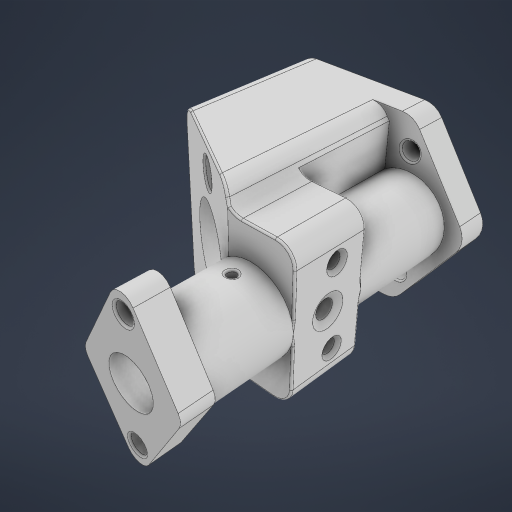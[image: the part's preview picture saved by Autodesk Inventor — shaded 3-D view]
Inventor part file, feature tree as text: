
AUTODESK INVENTOR PART (.ipt)
format: ipt  version: 2024.2 (Build 282272000, 272)  size: 712,192 bytes
history: native  units: mm
features: extrude x13, sketch x12, projected_geometry x12, fillet x9, chamfer x5, plane x1
ambient origin geometry x8: Origin, YZ Plane, XZ Plane, XY Plane, X Axis, Y Axis, Z Axis, Center Point
bodies: Solid1 (feature_tree)
feature tree (52):
  extrude  "Extrusion1"  Depth=22.5mm
  extrude  "Extrusion2"  Depth=16.134mm
  extrude  "Extrusion3"  Depth=5.0mm
  fillet  "Fillet1"  Radius=21.816616mm
  fillet  "Fillet3"  Radius=21.816616mm
  extrude  "Extrusion4"  Depth=6.0mm
  extrude  "Extrusion5"  Depth=8.0mm
  chamfer  "Chamfer1"  Distance=60.0mm
  chamfer  "Chamfer2"  Angle=120.0deg  [1 undecoded]
  chamfer  "Chamfer3"  Distance=49.469mm
  sketch  "Sketch6"  dims[d15=120.0deg]
  extrude  "Extrusion6"  Depth=0.5mm
  fillet  "Fillet4"  Radius=5.0mm
  extrude  "Extrusion7"  Depth=0.5mm
  fillet  "Fillet5"  [1 undecoded]
  sketch  "Sketch7"  dims[d16=120.0deg]
  plane  "Work Plane1"
  sketch  "Sketch8"  dims[d17=28.0mm]
  extrude  "Extrusion8"  TaperAngle=90.0deg  [1 undecoded]
  extrude  "Extrusion9"  Depth=0.5mm
  extrude  "Extrusion10"  Depth=0.5mm
  fillet  "Fillet6"  Radius=17.5mm
  chamfer  "Chamfer4"  Distance=10.0mm
  chamfer  "Chamfer5"  Distance=24.0mm
  fillet  "Fillet7"  Radius=2.5mm
  extrude  "Extrusion11"  Depth=0.5mm
  fillet  "Fillet8"  Radius=4.0mm
  fillet  "Fillet9"  Radius=7.5mm
  extrude  "Extrusion12"  Depth=0.5mm
  extrude  "Extrusion13"  Depth=0.5mm
  fillet  "Fillet10"  Radius=10.0mm
  sketch  "Sketch1"  dims[d0=12.5mm d1=22.5mm]
  sketch  "Sketch2"  dims[d2=16.134mm d3=16.134mm]
  projected_geometry  "Projected Loop1"
  sketch  "Sketch3"  dims[d4=5.0mm d5=5.0mm d6=21.816616mm d7=21.816616mm]
  projected_geometry  "Projected Loop2"
  sketch  "Sketch4"  dims[d8=40.0mm d9=6.0mm]
  projected_geometry  "Projected Loop3"
  projected_geometry  "Projected Loop4"
  sketch  "Sketch5"  dims[d10=8.0mm d11=0.0mm d12=22.5mm d13=60.0mm d14=0.0mm]
  projected_geometry  "Projected Loop5"
  projected_geometry  "Projected Loop6"
  projected_geometry  "Projected Loop7"
  projected_geometry  "Projected Loop8"
  projected_geometry  "Projected Loop9"
  sketch  "Sketch9"  dims[d18=0.0mm]
  projected_geometry  "Projected Loop10"
  sketch  "Sketch10"  dims[d19=10.0mm]
  projected_geometry  "Projected Loop11"
  projected_geometry  "Projected Loop12"
  sketch  "Sketch11"  dims[d20=8.0mm]
  sketch  "Sketch12"  dims[d21=120.0deg d22=120.0deg d23=49.469mm d24=0.0mm d25=5.0mm d27=5.0mm d28=4.999mm d29=90.0deg d30=90.0deg d31=14.0mm d32=7.0mm d33=17.5mm d34=0.0mm d35=10.0mm d36=24.0mm d37=0.0mm d38=1.0mm d39=2.5mm d40=6.108652mm d41=2.0mm d42=12.0mm d43=6.108652mm d44=4.0mm d45=4.0mm d46=6.108652mm d47=7.5mm d48=18.0mm d49=5.0mm d50=10.0mm d51=5.0mm d52=0.0mm d53=2.0mm d54=24.0mm d55=0.0mm d56=5.0mm d57=12.5mm d58=20.0mm d59=12.5mm d60=0.0mm d61=5.0mm d62=0.0mm d63=4.0mm d64=4.0mm d65=5.0mm d66=21.5mm d67=10.75mm d68=0.0mm d69=1.9mm d70=1.9mm d71=10.0mm d72=7.0mm d73=0.0mm d74=5.0mm d75=2.0mm d76=1.0mm d77=6.108652mm d78=1.0mm d79=1.0mm d80=6.108652mm d81=0.5mm d82=2.5mm d83=11.25mm d84=18.0mm d85=0.0mm d86=0.5mm d87=0.5mm d88=11.0mm d89=0.0mm d90=5.0mm d91=5.0mm d92=24.0mm d93=15.75mm d94=15.75mm d95=24.0mm d96=14.0mm d97=14.0mm d98=3.5mm d99=8.0mm d100=0.0mm d101=0.5mm]
note: 3 required parameter values undecoded (feature->parameter linkage not recoverable at this tier; creation-order binding heuristic only, values carry confidence <= 0.55)
